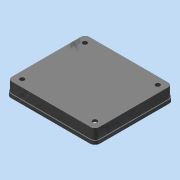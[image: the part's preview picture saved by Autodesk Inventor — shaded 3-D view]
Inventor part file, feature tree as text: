
AUTODESK INVENTOR PART (.ipt)
format: ipt  version: 2012 (Build 160160000, 160)  size: 157,696 bytes
history: native  units: in
note: dims shown in document units (in); Inventor stores cm internally (conversion verified against a paired STEP export)
features: extrude x4, sketch x4
ambient origin geometry x8: Origin, YZ Plane, XZ Plane, XY Plane, X Axis, Y Axis, Z Axis, Center Point
bodies: Solid1 (feature_tree)
feature tree (8):
  extrude  "Extrusion1"  Depth=4.0in
  extrude  "Extrusion2"  Depth=0.08in
  extrude  "Extrusion3"  Depth=0.04in
  extrude  "Extrusion4"  Depth=0.04in
  sketch  "Sketch2"  dims[d0=4.5in d1=4.0in]
  sketch  "Sketch3"  dims[d2=0.25in d3=0.08in]
  sketch  "Sketch5"  dims[d4=0.18in d5=0.0in d7=0.04in]
  sketch  "Sketch6"  dims[d8=0.04in d9=0.04in d10=0.04in d11=0.08in d12=0.4in d13=0.0in d14=0.12in d15=0.0in d16=0.23in d20=3.45in d21=0.37in d22=0.37in d23=0.12in d24=0.0in]
